# Revit family: GD10 3000-4000  x 1070 High Tables
name_source: partatom
category: Furniture
revit_build: Autodesk Revit 2016 (Build: 20161004_0715(x64)
units: mm (PartAtom-declared; Revit-internal decimal feet)

## family parameters
Always vertical = Yes
Cut with Voids When Loaded = No
OmniClass Number = 23.40.20.00
OmniClass Title = General Furniture and Specialties
Room Calculation Point = No
Shared = No
Work Plane-Based = No

## types (4) — shared parameters
1100 High Bottom Rail = Yes
Assembly Code = E2020200
Frame = Gresham - SOLID OAK
Height = 1070 mm  [stored 3.5105 ft]
Manufacturer = Gresham Office Furniture
Range = GD10
Table Top = Gresham - SOLID OAK
URL = www.gof.co.uk

## per-type parameters (varying)
| type | Depth | Product Code | Width |
| 3000 x 900 x 1070 | 900 mm  [stored 2.95276 ft] | GD10G1 | 3000 mm  [stored 9.84252 ft] |
| 3000 x 1200 x 1070 | 1200 mm  [stored 3.93701 ft] | GD10H1 | 3000 mm  [stored 9.84252 ft] |
| 4000 x 900 x 1070 | 900 mm  [stored 2.95276 ft] | GD10G2 | 4000 mm  [stored 13.1234 ft] |
| 4000 x 1200 x 1070 | 1200 mm  [stored 3.93701 ft] | GD10H2 | 4000 mm  [stored 13.1234 ft] |

note: [stored X ft] marks values corroborated as IEEE doubles in the binary element streams (Revit-internal decimal feet)

## geometry (parser evidence)
native form markers: Sweep x8
no freeform markers — native parametric forms only
